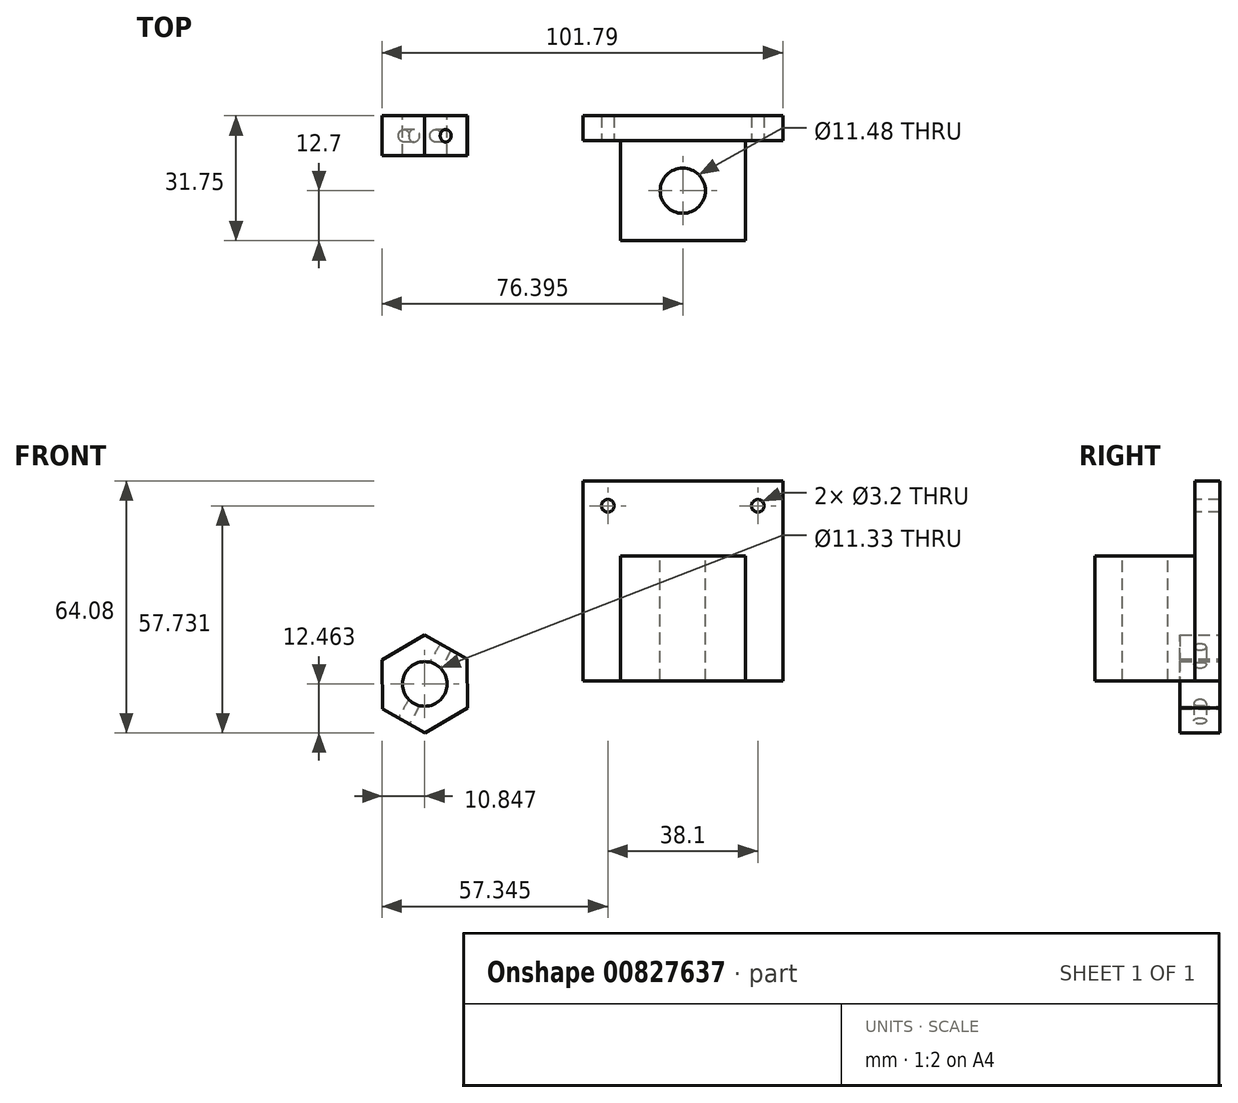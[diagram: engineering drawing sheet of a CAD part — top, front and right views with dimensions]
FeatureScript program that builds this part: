
annotation { "Feature Type Name" : "Feature", "Feature Type Description" : "" }
export const myFeature = defineFeature(function(context is Context, id is Id, definition is map)
    precondition{}
    {
        {
            var Q0;
            Q0=qCreatedBy(makeId("Front.planeOp"),FACE);
            var sketch = newSketch(context, id + "F0", { "sketchPlane" : qUnion([Q0])});
            skLineSegment(sketch, "E0.bottom", {"start": v(-12, 32.51) * mm, "end": v(38.8, 32.51) * mm});
            skLineSegment(sketch, "E0.top", {"start": v(-12, -18.29) * mm, "end": v(38.8, -18.29) * mm});
            skLineSegment(sketch, "E0.left", {"start": v(-12, 32.51) * mm, "end": v(-12, -18.29) * mm});
            skLineSegment(sketch, "E0.right", {"start": v(38.8, 32.51) * mm, "end": v(38.8, -18.29) * mm});
            skSolve(sketch);
        }
        {
            var Q0;
            Q0=makeQuery(id+"F0.imprint","IMPRINT",FACE,{"disambiguationData":[TD([[makeQuery(id+"F0.imprint","IMPRINT",EDGE,{"derivedFrom":sQuery(id+"F0.wireOp",EDGE,"E0.bottom")}),-1.0]])]});
            extrude(context, id + "F1", {"entities" : qUnion([Q0]), "depth" : 6.35 * mm, "offsetDistance" : 25.4 * mm});
        }
        {
            var Q0;
            Q0=makeQuery(id+"F1.opExtrude","CAP_FACE",FACE,{"disambiguationData":[OSD([sQuery(id+"F0.wireOp",EDGE,"E0.bottom"),sQuery(id+"F0.wireOp",EDGE,"E0.top"),sQuery(id+"F0.wireOp",EDGE,"E0.left"),sQuery(id+"F0.wireOp",EDGE,"E0.right")])],"isStart":false});
            var sketch = newSketch(context, id + "F2", { "sketchPlane" : qUnion([Q0])});
            skLineSegment(sketch, "E1.bottom", {"start": v(-2.47, -18.29) * mm, "end": v(29.28, -18.29) * mm});
            skLineSegment(sketch, "E1.top", {"start": v(-2.47, 13.46) * mm, "end": v(29.28, 13.46) * mm});
            skLineSegment(sketch, "E1.left", {"start": v(-2.47, -18.29) * mm, "end": v(-2.47, 13.46) * mm});
            skLineSegment(sketch, "E1.right", {"start": v(29.28, -18.29) * mm, "end": v(29.28, 13.46) * mm});
            skSolve(sketch);
        }
        {
            var Q0;
            Q0=makeQuery(id+"F2.imprint","IMPRINT",FACE,{"disambiguationData":[TD([[makeQuery(id+"F2.imprint","IMPRINT",EDGE,{"derivedFrom":sQuery(id+"F2.wireOp",EDGE,"E1.bottom")}),1.0]])]});
            extrude(context, id + "F3", {"entities" : qUnion([Q0]), "operationType" : NewBodyOperationType.ADD, "depth" : 25.4 * mm, "offsetDistance" : 25.4 * mm});
        }
        {
            var Q0;
            Q0=makeQuery(id+"F3.opExtrude","SWEPT_FACE",FACE,{"disambiguationData":[OSD([sQuery(id+"F2.wireOp",EDGE,"E1.top")])]});
            var sketch = newSketch(context, id + "F4", { "sketchPlane" : qUnion([Q0])});
            skCircle(sketch, "E2", {"center": v(13.4, -19.05) * mm, "radius": 5.74 * mm});
            skPoint(sketch, "E2.centerSnap0", {"position": v(-2.47, -19.05) * mm});
            skPoint(sketch, "E2.centerSnap1", {"position": v(13.4, -31.75) * mm});
            skSolve(sketch);
        }
        {
            var Q0;
            Q0=makeQuery(id+"F4.imprint","IMPRINT",FACE,{"disambiguationData":[TD([[makeQuery(id+"F4.imprint","IMPRINT",EDGE,{"derivedFrom":sQuery(id+"F4.wireOp",EDGE,"E2")}),1.0]])]});
            extrude(context, id + "F5", {"entities" : qUnion([Q0]), "operationType" : NewBodyOperationType.REMOVE, "oppositeDirection" : true, "depth" : 33.02 * mm, "offsetDistance" : 25.4 * mm});
        }
        {
            var Q0;
            Q0=makeQuery(id+"F1.opExtrude","CAP_FACE",FACE,{"disambiguationData":[OSD([sQuery(id+"F0.wireOp",EDGE,"E0.bottom"),sQuery(id+"F0.wireOp",EDGE,"E0.top"),sQuery(id+"F0.wireOp",EDGE,"E0.left"),sQuery(id+"F0.wireOp",EDGE,"E0.right")])],"isStart":false});
            var sketch = newSketch(context, id + "F6", { "sketchPlane" : qUnion([Q0])});
            skCircle(sketch, "E3", {"center": v(32.45, 26.16) * mm, "radius": 1.6 * mm});
            skCircle(sketch, "E4", {"center": v(-5.65, 26.16) * mm, "radius": 1.6 * mm});
            skSolve(sketch);
        }
        {
            var Q0;
            Q0=makeQuery(id+"F6.imprint","IMPRINT",FACE,{"disambiguationData":[TD([[makeQuery(id+"F6.imprint","IMPRINT",EDGE,{"derivedFrom":sQuery(id+"F6.wireOp",EDGE,"E4")}),1.0]])]});
            var Q1;
            Q1=makeQuery(id+"F6.imprint","IMPRINT",FACE,{"disambiguationData":[TD([[makeQuery(id+"F6.imprint","IMPRINT",EDGE,{"derivedFrom":sQuery(id+"F6.wireOp",EDGE,"E3")}),1.0]])]});
            extrude(context, id + "F7", {"entities" : qUnion([Q0, Q1]), "operationType" : NewBodyOperationType.REMOVE, "oppositeDirection" : true, "depth" : 6.6 * mm, "offsetDistance" : 25.4 * mm});
        }
        {
            var Q0;
            Q0=qCreatedBy(makeId("Front.planeOp"),FACE);
            var sketch = newSketch(context, id + "F8", { "sketchPlane" : qUnion([Q0])});
            skCircle(sketch, "E5.cCircle", {"center": v(-52.14, -19.1) * mm, "radius": 10.8 * mm, "construction": true});
            skLineSegment(sketch, "E5.0", {"start": v(-52.26, -6.64) * mm, "end": v(-41.4, -12.78) * mm});
            skLineSegment(sketch, "E5.1", {"start": v(-41.4, -12.78) * mm, "end": v(-41.3, -25.24) * mm});
            skLineSegment(sketch, "E5.2", {"start": v(-41.3, -25.24) * mm, "end": v(-52.03, -31.57) * mm});
            skLineSegment(sketch, "E5.3", {"start": v(-52.03, -31.57) * mm, "end": v(-62.88, -25.44) * mm});
            skLineSegment(sketch, "E5.4", {"start": v(-62.88, -25.44) * mm, "end": v(-63, -12.97) * mm});
            skLineSegment(sketch, "E5.5", {"start": v(-63, -12.97) * mm, "end": v(-52.26, -6.64) * mm});
            skPoint(sketch, "E5.0.midPoint", {"position": v(-46.83, -9.7) * mm});
            skCircle(sketch, "E6", {"center": v(-52.14, -19.1) * mm, "radius": 5.66 * mm});
            skSolve(sketch);
        }
        {
            var Q0;
            Q0=makeQuery(id+"F8.imprint","IMPRINT",FACE,{"disambiguationData":[TD([[makeQuery(id+"F8.imprint","IMPRINT",EDGE,{"derivedFrom":sQuery(id+"F8.wireOp",EDGE,"E5.0")}),-1.0]])]});
            extrude(context, id + "F9", {"entities" : qUnion([Q0]), "depth" : 10.16 * mm, "offsetDistance" : 25.4 * mm});
        }
        {
            var Q0;
            Q0=makeQuery(id+"F9.opExtrude","SWEPT_FACE",FACE,{"disambiguationData":[OSD([sQuery(id+"F8.wireOp",EDGE,"E5.3")])]});
            var sketch = newSketch(context, id + "F10", { "sketchPlane" : qUnion([Q0])});
            skCircle(sketch, "E7", {"center": v(-36, 5.08) * mm, "radius": 1.6 * mm});
            skPoint(sketch, "E7.centerSnap0", {"position": v(-29.76, 5.08) * mm});
            skPoint(sketch, "E7.centerSnap1", {"position": v(-36, 10.16) * mm});
            skSolve(sketch);
        }
        {
            var Q0;
            Q0=makeQuery(id+"F10.imprint","IMPRINT",FACE,{"disambiguationData":[TD([[makeQuery(id+"F10.imprint","IMPRINT",EDGE,{"derivedFrom":sQuery(id+"F10.wireOp",EDGE,"E7")}),1.0]])]});
            extrude(context, id + "F11", {"entities" : qUnion([Q0]), "operationType" : NewBodyOperationType.REMOVE, "oppositeDirection" : true, "depth" : 22.86 * mm, "offsetDistance" : 25.4 * mm});
        }
    });
